# Revit family: Haworth_Mexique_Stool
name_source: partatom
category: Furniture
revit_build: Autodesk Revit 2018 (Build: 20170223_1515(x64)
units: mm (PartAtom-declared; Revit-internal decimal feet)

## family parameters
Always vertical = Yes
Cut with Voids When Loaded = No
OmniClass Number = 23.40.70.14.64.21
OmniClass Title = Systems Furniture
Room Calculation Point = No
Shared = No
Work Plane-Based = No

## types (2) — shared parameters
Assembly Code = E2020200
Footrest Finish = Haworth _ Paint _ Undecided _ Seating
Manufacturer = Haworth
Model = HCCSMXS
Revision Number = 1
Size = Verify Final Dim. w/ Haworth
Sustainability Info = https://www.haworth.com
URL = https://www.haworth.com
URL - Product = https://www.haworth.com
Warranty = http://www.haworth.com

## per-type parameters (varying)
| type | Actual Depth | Actual Height | Actual Width | Description | High | Low |
| Low Stool | 12.6 " | 17.7 " | 15.75 " | Haworth - Cassina - Mexique - Stool - Low | No | Yes |
| High Stool | 14.6 " | 28.3 " | 18.5 " | Haworth - Cassina - Mexique - Stool - High | Yes | No |

## geometry (parser evidence)
native form markers: Sweep x11
no freeform markers — native parametric forms only
